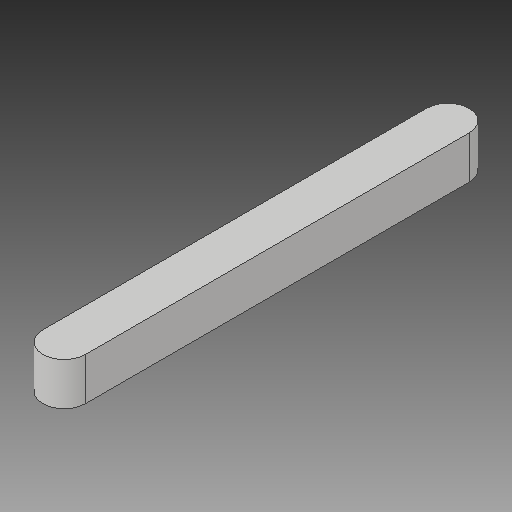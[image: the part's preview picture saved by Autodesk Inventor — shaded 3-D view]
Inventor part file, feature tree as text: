
AUTODESK INVENTOR PART (.ipt)
format: ipt  version: 2017 (Build 210142000, 142)  size: 70,656 bytes
history: native  units: in
note: dims shown in document units (in); Inventor stores cm internally (conversion verified against a paired STEP export)
features: fillet x1
ambient origin geometry x8: Origin, YZ Plane, XZ Plane, XY Plane, X Axis, Y Axis, Z Axis, Center Point
bodies: Solid1 (feature_tree)
feature tree (1):
  fillet  "Fillet1"  [1 undecoded]
note: 1 required parameter value undecoded (feature->parameter linkage not recoverable at this tier; creation-order binding heuristic only, values carry confidence <= 0.55)
